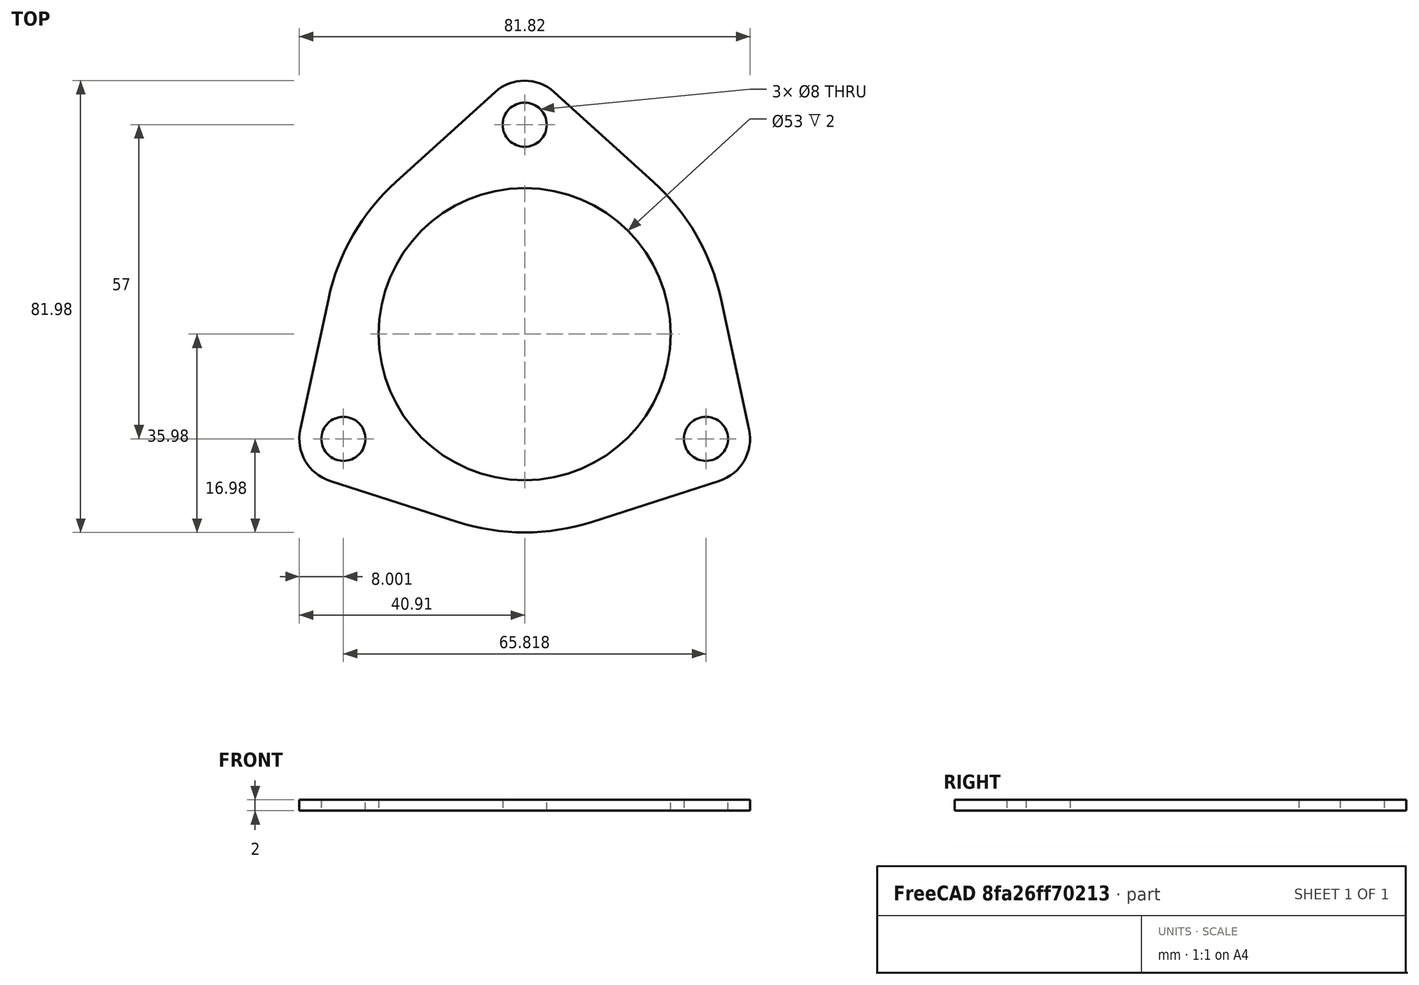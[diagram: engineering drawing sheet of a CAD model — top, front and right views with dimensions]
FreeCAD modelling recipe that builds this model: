
FCSTD DOCUMENT  (FreeCAD 0.21R33771 (Git))
Label: item_02
License: All rights reserved
LicenseURL: http://en.wikipedia.org/wiki/All_rights_reserved
objects: TechDraw::DrawViewDimension×7, TechDraw::DrawViewPart×3, Image::ImagePlane×1, Sketcher::SketchObject×1, PartDesign::Pad×1, PartDesign::Fillet×1, PartDesign::Body×1, TechDraw::DrawSVGTemplate×1, TechDraw::DrawPage×1
note: 15 computed .brp shape members not serialized (recipe doc carries the construction recipe); baked Part::Feature solids carry a one-line shape summary decoded from their .brp

FEATURE [Image::ImagePlane] triangle_flange_500x500  label="triangle-flange-500x500"
  Placement = pos=(1.35922,-1.77554,0) rot=(0,0,-1;0.453786rad)
  XSize = 138.141
  YSize = 138.141
FEATURE [Sketcher::SketchObject] Sketch
  FullyConstrained = true
  MapMode = 5
  Support = -> [XY_Plane]
  sketch-geometry (19):
    g0: Circle CenterX=0 CenterY=0 CenterZ=0 NormalX=0 NormalY=0 NormalZ=1 AngleXU=0 Radius=26.5
    g1: ArcOfCircle CenterX=0 CenterY=38 CenterZ=0 NormalX=0 NormalY=0 NormalZ=1 AngleXU=0 Radius=8 StartAngle=0.835084 EndAngle=2.30651
    g2: ArcOfCircle CenterX=32.909 CenterY=-19 CenterZ=0 NormalX=0 NormalY=0 NormalZ=1 AngleXU=0 Radius=8 StartAngle=5.02387 EndAngle=6.4953
    g3: ArcOfCircle CenterX=-32.909 CenterY=-19 CenterZ=0 NormalX=0 NormalY=0 NormalZ=1 AngleXU=0 Radius=8 StartAngle=2.92948 EndAngle=4.4009
    g4: Circle CenterX=0 CenterY=38 CenterZ=0 NormalX=0 NormalY=0 NormalZ=1 AngleXU=0 Radius=4
    g5: Circle CenterX=32.909 CenterY=-19 CenterZ=0 NormalX=0 NormalY=0 NormalZ=1 AngleXU=0 Radius=4
    g6: Circle CenterX=-32.909 CenterY=-19 CenterZ=0 NormalX=0 NormalY=0 NormalZ=1 AngleXU=0 Radius=4
    g7: LineSegment StartX=0 StartY=0 StartZ=0 EndX=-32.909 EndY=-19 EndZ=0
    g8: LineSegment StartX=0 StartY=0 StartZ=0 EndX=32.909 EndY=-19 EndZ=0
    g9: LineSegment StartX=0 StartY=0 StartZ=0 EndX=0 EndY=38 EndZ=0
    g10: LineSegment StartX=0 StartY=0 StartZ=0 EndX=-32.909 EndY=19 EndZ=0
    g11: LineSegment StartX=0 StartY=0 StartZ=0 EndX=32.909 EndY=19 EndZ=0
    g12: LineSegment StartX=0 StartY=0 StartZ=0 EndX=0 EndY=-38 EndZ=0
    g13: LineSegment StartX=32.909 StartY=19 StartZ=0 EndX=40.7297 EndY=-17.3158 EndZ=0
    g14: LineSegment StartX=32.909 StartY=19 StartZ=0 EndX=5.36892 EndY=43.9308 EndZ=0
    g15: LineSegment StartX=-32.909 StartY=19 StartZ=0 EndX=-5.36892 EndY=43.9308 EndZ=0
    g16: LineSegment StartX=-32.909 StartY=19 StartZ=0 EndX=-40.7297 EndY=-17.3158 EndZ=0
    g17: LineSegment StartX=-35.3607 StartY=-26.615 StartZ=0 EndX=0 EndY=-38 EndZ=0
    g18: LineSegment StartX=0 StartY=-38 StartZ=0 EndX=35.3607 EndY=-26.615 EndZ=0
  constraints (49):
    c: Coincident(g0,g-1)
    c: Coincident(g5,g2)
    c: Coincident(g6,g3)
    c: Coincident(g4,g1)
    c: Coincident(g7,g0)
    c: Coincident(g7,g3)
    c: Coincident(g8,g0)
    c: Coincident(g8,g2)
    c: Coincident(g9,g0)
    c: Coincident(g9,g1)
    c: Angle(g7,g8) = 2.0944
    c: Angle(g8,g9) = 2.0944
    c: Equal(g7,g8)
    c: Equal(g8,g9)
    c: Distance(g9) = 38
    c: Vertical(g9)
    c: Coincident(g10,g0)
    c: Coincident(g11,g0)
    c: Coincident(g12,g0)
    c: Angle(g11,g7) = 3.14159
    c: Angle(g10,g8) = 3.14159
    c: Angle(g12,g9) = 3.14159
    c: Distance(g11) = 38
    c: Equal(g11,g10)
    c: Equal(g10,g12)
    c: Diameter(g1) = 16
    c: Diameter(g4) = 8
    c: Equal(g1,g2)
    c: Equal(g2,g3)
    c: Equal(g5,g6)
    c: Equal(g6,g4)
    c: Diameter(g0) = 53
    c: Coincident(g13,g11)
    c: Coincident(g14,g11)
    c: Coincident(g15,g10)
    c: Coincident(g16,g10)
    c: Coincident(g17,g12)
    c: Coincident(g18,g12)
    c: Equal(g18,g17)
    c: Equal(g17,g16)
    c: Equal(g16,g15)
    c: Equal(g15,g14)
    c: Equal(g14,g13)
    c: Coincident(g3,g16)
    c: Coincident(g3,g17)
    c: Coincident(g2,g13)
    c: Coincident(g2,g18)
    c: Coincident(g1,g14)
    c: Tangent(g1,g15) = 1.5708
FEATURE [PartDesign::Pad] Pad
  Direction = (0,0,1)
  Length = 2
  Length2 = 10
  Midplane = true
  Profile = -> Sketch
  ReferenceAxis = -> Sketch [N_Axis]
  Type = 0
FEATURE [PartDesign::Fillet] Fillet
  Base = -> Pad [Edge1,Edge17,Edge8]
  BaseFeature = -> Pad
  Radius = 40
  SupportTransform = false
  UseAllEdges = false
FEATURE [PartDesign::Body] Body
  Group = -> [Sketch,Pad,Fillet]
  Origin = -> Origin
  Tip = -> Fillet
FEATURE [TechDraw::DrawSVGTemplate] Template
  EditableTexts = Designed_by_Name=Reza Heshmati; Drawing_number=item_02; FC-Date=Date; FC-SC=Scale; FC-SH=Sheet; FC-Title=Item #2; Subtitle=Subtitle; Weight=Weight
  Height = 210
  Orientation = 1
  Template = <path>
  Width = 297
FEATURE [TechDraw::DrawViewPart] View
  Caption = 3D View
  CoarseView = false
  Direction = (0.57735,-0.57735,0.57735)
  Focus = 100
  HardHidden = false
  IsoCount = 0
  IsoHidden = false
  IsoVisible = false
  LockPosition = false
  Perspective = false
  Rotation = 0
  ScaleType = 0
  ScrubCount = 0
  SeamHidden = false
  SeamVisible = false
  SmoothHidden = false
  SmoothVisible = true
  Source = -> [Body]
  X = 76.4655
  XDirection = (0.707107,0.707107,0)
  Y = 57.7615
FEATURE [TechDraw::DrawViewPart] View001
  Caption = Top View
  CoarseView = false
  Direction = (0,0,1)
  Focus = 100
  HardHidden = false
  IsoCount = 0
  IsoHidden = false
  IsoVisible = false
  LockPosition = false
  Perspective = false
  Rotation = 0
  Scale = 0.8
  ScaleType = 2
  ScrubCount = 0
  SeamHidden = false
  SeamVisible = false
  SmoothHidden = false
  SmoothVisible = true
  Source = -> [Body]
  X = 99.4539
  XDirection = (1,0,0)
  Y = 144.311
FEATURE [TechDraw::DrawViewPart] View002
  Caption = Side View
  CoarseView = false
  Direction = (0,-1,0)
  Focus = 100
  HardHidden = false
  IsoCount = 0
  IsoHidden = false
  IsoVisible = false
  LockPosition = false
  Perspective = false
  Rotation = 0
  Scale = 0.8
  ScaleType = 2
  ScrubCount = 0
  SeamHidden = false
  SeamVisible = false
  SmoothHidden = false
  SmoothVisible = true
  Source = -> [Body]
  X = 222.627
  XDirection = (1,0,0)
  Y = 133.505
FEATURE [TechDraw::DrawViewDimension] Dimension
  AngleOverride = false
  Arbitrary = false
  ArbitraryTolerances = false
  EqualTolerance = true
  ExtensionAngle = 0
  FormatSpec = ⌀%.2w
  FormatSpecOverTolerance = %+.2w
  FormatSpecUnderTolerance = %+.2w
  Inverted = false
  LineAngle = 0
  LockPosition = false
  MeasureType = 1
  OverTolerance = 0
  References2D = -> [View001]
  Rotation = 0
  ScaleType = 0
  TheoreticalExact = false
  Type = 5
  UnderTolerance = 0
  X = 45.1525
  Y = 10.9401
FEATURE [TechDraw::DrawViewDimension] Dimension001
  AngleOverride = false
  Arbitrary = false
  ArbitraryTolerances = false
  EqualTolerance = true
  ExtensionAngle = 0
  FormatSpec = ⌀%.2w
  FormatSpecOverTolerance = %+.2w
  FormatSpecUnderTolerance = %+.2w
  Inverted = false
  LineAngle = 0
  LockPosition = false
  MeasureType = 1
  OverTolerance = 0
  References2D = -> [View001]
  Rotation = 0
  ScaleType = 0
  TheoreticalExact = false
  Type = 5
  UnderTolerance = 0
  X = 18.3315
  Y = 38.0975
FEATURE [TechDraw::DrawViewDimension] Dimension002
  AngleOverride = false
  Arbitrary = false
  ArbitraryTolerances = false
  EqualTolerance = true
  ExtensionAngle = 0
  FormatSpec = ⌀%.2w
  FormatSpecOverTolerance = %+.2w
  FormatSpecUnderTolerance = %+.2w
  Inverted = false
  LineAngle = 0
  LockPosition = false
  MeasureType = 1
  OverTolerance = 0
  References2D = -> [View001]
  Rotation = 0
  ScaleType = 0
  TheoreticalExact = false
  Type = 5
  UnderTolerance = 0
  X = 46.6374
  Y = -23.1929
FEATURE [TechDraw::DrawViewDimension] Dimension003
  AngleOverride = false
  Arbitrary = false
  ArbitraryTolerances = false
  EqualTolerance = true
  ExtensionAngle = 0
  FormatSpec = ⌀%.2w
  FormatSpecOverTolerance = %+.2w
  FormatSpecUnderTolerance = %+.2w
  Inverted = false
  LineAngle = 0
  LockPosition = false
  MeasureType = 1
  OverTolerance = 0
  References2D = -> [View001]
  Rotation = 0
  ScaleType = 0
  TheoreticalExact = false
  Type = 5
  UnderTolerance = 0
  X = 35.6821
  Y = 22.0225
FEATURE [TechDraw::DrawViewDimension] Dimension004
  AngleOverride = false
  Arbitrary = false
  ArbitraryTolerances = false
  EqualTolerance = true
  ExtensionAngle = 0
  FormatSpec = %.2w
  FormatSpecOverTolerance = %+.2w
  FormatSpecUnderTolerance = %+.2w
  Inverted = false
  LineAngle = 0
  LockPosition = false
  MeasureType = 1
  OverTolerance = 0
  References2D = -> [View001]
  Rotation = 0
  ScaleType = 0
  TheoreticalExact = false
  Type = 0
  UnderTolerance = 0
  X = -43.8223
  Y = -2.02903
FEATURE [TechDraw::DrawViewDimension] Dimension005
  AngleOverride = false
  Arbitrary = false
  ArbitraryTolerances = false
  EqualTolerance = true
  ExtensionAngle = 0
  FormatSpec = %.2w
  FormatSpecOverTolerance = %+.2w
  FormatSpecUnderTolerance = %+.2w
  Inverted = false
  LineAngle = 0
  LockPosition = false
  MeasureType = 1
  OverTolerance = 0
  References2D = -> [View001]
  Rotation = 0
  ScaleType = 0
  TheoreticalExact = false
  Type = 2
  UnderTolerance = 0
  X = -36.1937
  Y = 16.6116
FEATURE [TechDraw::DrawViewDimension] Dimension006
  AngleOverride = false
  Arbitrary = false
  ArbitraryTolerances = false
  EqualTolerance = true
  ExtensionAngle = 0
  FormatSpec = %.2w
  FormatSpecOverTolerance = %+.2w
  FormatSpecUnderTolerance = %+.2w
  Inverted = false
  LineAngle = 0
  LockPosition = false
  MeasureType = 1
  OverTolerance = 0
  References2D = -> [View002]
  Rotation = 0
  ScaleType = 0
  TheoreticalExact = false
  Type = 2
  UnderTolerance = 0
  X = -48.0805
  Y = 3.05004
FEATURE [TechDraw::DrawPage] Page
  KeepUpdated = true
  NextBalloonIndex = 1
  ProjectionType = 0
  Template = -> Template
  Views = -> [View,View001,View002,Dimension,Dimension001,Dimension002,Dimension003,Dimension004,Dimension005,Dimension006]
note: 1 file-system path scrubbed to <path> (originals preserved in the JSON sidecar)
